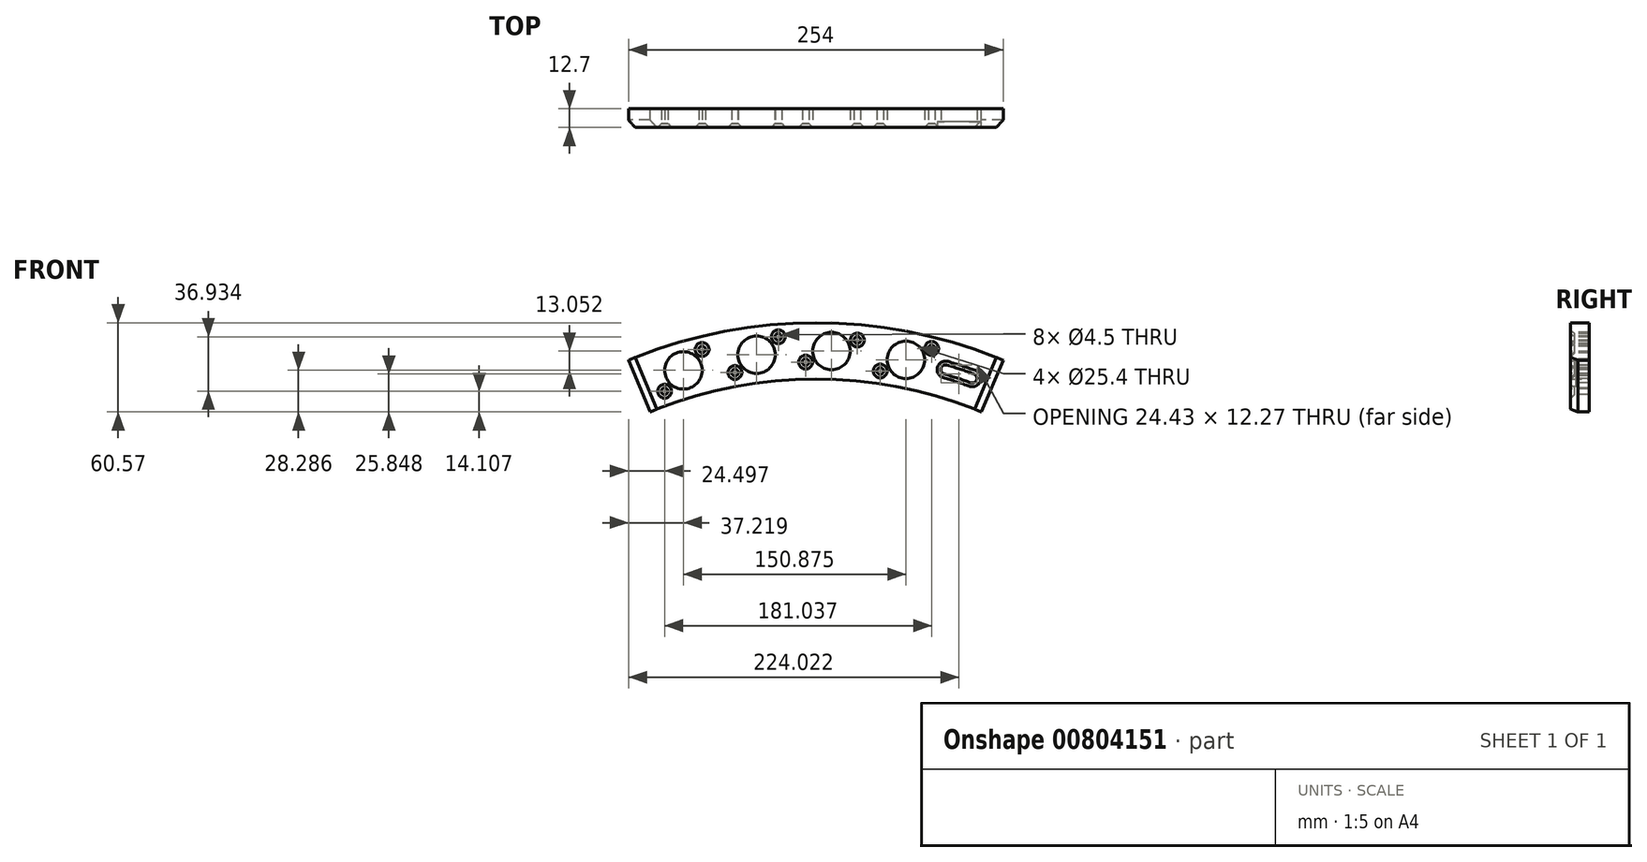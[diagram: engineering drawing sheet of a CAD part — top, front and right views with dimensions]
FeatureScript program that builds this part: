
annotation { "Feature Type Name" : "Feature", "Feature Type Description" : "" }
export const myFeature = defineFeature(function(context is Context, id is Id, definition is map)
    precondition{}
    {
        {
            var Q0;
            Q0=qCreatedBy(makeId("Front.planeOp"),FACE);
            var sketch = newSketch(context, id + "F0", { "sketchPlane" : qUnion([Q0])});
            skLineSegment(sketch, "E0", {"start": v(-127, 0) * mm, "end": v(127, 0) * mm, "construction": true});
            skArc(sketch, "E1", {"start": v(127, 0) * mm, "mid": v(0, 25.4) * mm, "end": v(-127, 0) * mm});
            skArc(sketch, "E2.0", {"start": v(112.35, -35.17) * mm, "mid": v(0, -12.7) * mm, "end": v(-112.35, -35.17) * mm});
            skLineSegment(sketch, "E3", {"start": v(-127, 0) * mm, "end": v(-112.35, -35.17) * mm});
            skLineSegment(sketch, "E4", {"start": v(127, 0) * mm, "end": v(112.35, -35.17) * mm});
            skSolve(sketch);
        }
        {
            var Q0;
            Q0=qSketchRegion(id+"F0",true);
            extrude(context, id + "F1", {"entities" : qUnion([Q0]), "depth" : 12.7 * mm, "offsetDistance" : 25.4 * mm});
        }
        {
            var Q0;
            Q0=makeQuery(id+"F1.opExtrude","CAP_FACE",FACE,{"disambiguationData":[OSD([sQuery(id+"F0.wireOp",EDGE,"E1"),sQuery(id+"F0.wireOp",EDGE,"E2.0"),sQuery(id+"F0.wireOp",EDGE,"E3"),sQuery(id+"F0.wireOp",EDGE,"E4")])],"isStart":false});
            var sketch = newSketch(context, id + "F2", { "sketchPlane" : qUnion([Q0])});
            skLineSegment(sketch, "E5", {"start": v(0, 25.4) * mm, "end": v(0, -12.7) * mm, "construction": true});
            skPoint(sketch, "E6", {"position": v(0, 6.35) * mm});
            skArc(sketch, "E7", {"start": v(119.67, -17.58) * mm, "mid": v(0, 6.35) * mm, "end": v(-119.67, -17.58) * mm, "construction": true});
            skCircle(sketch, "E8", {"center": v(61.1, 0.3) * mm, "radius": 12.7 * mm});
            skCircle(sketch, "E9", {"center": v(-89.78, -6.88) * mm, "radius": 12.7 * mm});
            skLineSegment(sketch, "E10", {"start": v(-119.67, -17.58) * mm, "end": v(-89.78, -6.88) * mm, "construction": true});
            skCircle(sketch, "E11", {"center": v(10.64, 6.17) * mm, "radius": 12.7 * mm});
            skCircle(sketch, "E12", {"center": v(-40.1, 3.75) * mm, "radius": 12.7 * mm});
            skLineSegment(sketch, "E13", {"start": v(-89.78, -6.88) * mm, "end": v(-40.1, 3.75) * mm, "construction": true});
            skLineSegment(sketch, "E14", {"start": v(10.64, 6.17) * mm, "end": v(61.1, 0.3) * mm, "construction": true});
            skLineSegment(sketch, "E15", {"start": v(-40.1, 3.75) * mm, "end": v(10.64, 6.17) * mm, "construction": true});
            skSolve(sketch);
        }
        {
            var Q0;
            Q0=qSketchRegion(id+"F2",true);
            extrude(context, id + "F3", {"entities" : qUnion([Q0]), "operationType" : NewBodyOperationType.REMOVE, "endBound" : BoundingType.THROUGH_ALL, "oppositeDirection" : true, "depth" : 25.4 * mm, "offsetDistance" : 25.4 * mm});
        }
        {
            var Q0;
            Q0=makeQuery(id+"F1.opExtrude","CAP_EDGE",EDGE,{"disambiguationData":[OSD([sQuery(id+"F0.wireOp",EDGE,"E3")])],"isStart":false});
            var Q1;
            Q1=makeQuery(id+"F1.opExtrude","CAP_EDGE",EDGE,{"disambiguationData":[OSD([sQuery(id+"F0.wireOp",EDGE,"E4")])],"isStart":false});
            chamfer(context, id + "F4", {"entities" : qUnion([Q0, Q1]), "width" : 5.08 * mm, "tangentPropagation" : true});
        }
        {
            var Q0;
            Q0=makeQuery(id+"F1.opExtrude","CAP_FACE",FACE,{"disambiguationData":[OSD([sQuery(id+"F0.wireOp",EDGE,"E1"),sQuery(id+"F0.wireOp",EDGE,"E2.0"),sQuery(id+"F0.wireOp",EDGE,"E3"),sQuery(id+"F0.wireOp",EDGE,"E4")])],"isStart":false});
            var sketch = newSketch(context, id + "F5", { "sketchPlane" : qUnion([Q0])});
            skCircle(sketch, "E16.0", {"center": v(10.64, 6.17) * mm, "radius": 12.7 * mm, "construction": true});
            skPoint(sketch, "E17", {"position": v(-6.88, -1.32) * mm});
            skLineSegment(sketch, "E18", {"start": v(10.64, 6.17) * mm, "end": v(-6.88, -1.32) * mm, "construction": true});
            skLineSegment(sketch, "E19", {"start": v(10.64, 6.17) * mm, "end": v(28.15, 13.66) * mm, "construction": true});
            skPoint(sketch, "E20", {"position": v(28.15, 13.66) * mm});
            skCircle(sketch, "E21.0", {"center": v(61.1, 0.3) * mm, "radius": 12.7 * mm});
            skLineSegment(sketch, "E22", {"start": v(61.1, 0.3) * mm, "end": v(78.53, 7.96) * mm, "construction": true});
            skLineSegment(sketch, "E23", {"start": v(61.1, 0.3) * mm, "end": v(43.66, -7.37) * mm, "construction": true});
            skPoint(sketch, "E24", {"position": v(43.66, -7.37) * mm});
            skPoint(sketch, "E25", {"position": v(78.53, 7.96) * mm});
            skCircle(sketch, "E26.1", {"center": v(-89.78, -6.88) * mm, "radius": 12.7 * mm});
            skCircle(sketch, "E26.2", {"center": v(-40.1, 3.75) * mm, "radius": 12.7 * mm});
            skLineSegment(sketch, "E27", {"start": v(-54.8, -8.36) * mm, "end": v(-40.1, 3.75) * mm});
            skLineSegment(sketch, "E28", {"start": v(-40.1, 3.75) * mm, "end": v(-25.4, 15.87) * mm});
            skLineSegment(sketch, "E29", {"start": v(-89.78, -6.88) * mm, "end": v(-102.5, -21.06) * mm});
            skLineSegment(sketch, "E30", {"start": v(-89.78, -6.88) * mm, "end": v(-77.06, 7.3) * mm});
            skPoint(sketch, "E31", {"position": v(-102.5, -21.06) * mm});
            skPoint(sketch, "E32", {"position": v(-77.06, 7.3) * mm});
            skPoint(sketch, "E33", {"position": v(-54.8, -8.36) * mm});
            skPoint(sketch, "E34", {"position": v(-25.4, 15.87) * mm});
            skSolve(sketch);
        }
        {
            var Q0;
            Q0=sQuery(id+"F5.wireOp",VERTEX,"E17");
            var Q1;
            Q1=sQuery(id+"F5.wireOp",VERTEX,"E20");
            var Q2;
            Q2=sQuery(id+"F5.wireOp",VERTEX,"E24");
            var Q3;
            Q3=sQuery(id+"F5.wireOp",VERTEX,"E25");
            var Q4;
            Q4=sQuery(id+"F5.wireOp",VERTEX,"E32");
            var Q5;
            Q5=sQuery(id+"F5.wireOp",VERTEX,"E31");
            var Q6;
            Q6=sQuery(id+"F5.wireOp",VERTEX,"E33");
            var Q7;
            Q7=sQuery(id+"F5.wireOp",VERTEX,"E34");
            var Q8;
            Q8=makeQuery(id+"F1.opExtrude","SWEPT_BODY",BODY,{"disambiguationData":[OSD([sQuery(id+"F0.wireOp",EDGE,"E1"),sQuery(id+"F0.wireOp",EDGE,"E2.0"),sQuery(id+"F0.wireOp",EDGE,"E3"),sQuery(id+"F0.wireOp",EDGE,"E4")])]});
            hole(context, id + "F6", {"style" : HoleStyle.C_SINK, "endStyle" : HoleEndStyle.THROUGH, "holeDiameter" : 4.5 * mm, "cSinkDiameter" : 9.4 * mm, "cSinkAngle" : 82 * degree, "majorDiameter" : 6.35 * mm, "tappedDepth" : 9.52 * mm, "tapClearance" : 3, "startFromSketch" : true, "locations" : qUnion([Q0, Q1, Q2, Q3, Q4, Q5, Q6, Q7]), "scope" : qUnion([Q8])});
        }
        {
            var Q0;
            Q0=makeQuery(id+"F1.opExtrude","CAP_FACE",FACE,{"disambiguationData":[OSD([sQuery(id+"F0.wireOp",EDGE,"E1"),sQuery(id+"F0.wireOp",EDGE,"E2.0"),sQuery(id+"F0.wireOp",EDGE,"E3"),sQuery(id+"F0.wireOp",EDGE,"E4")])],"isStart":false});
            var sketch = newSketch(context, id + "F7", { "sketchPlane" : qUnion([Q0])});
            skArc(sketch, "E35.0", {"start": v(114.97, -15.67) * mm, "mid": v(0.17, 6.35) * mm, "end": v(-114.66, -15.55) * mm, "construction": true});
            skLineSegment(sketch, "E36", {"start": v(107.64, -33.26) * mm, "end": v(114.97, -15.67) * mm, "construction": true});
            skArc(sketch, "E37.0", {"start": v(107.15, -9.3) * mm, "mid": v(98.05, -6.16) * mm, "end": v(88.86, -3.3) * mm});
            skArc(sketch, "E38.0", {"start": v(113.8, -18.62) * mm, "mid": v(113.77, -18.6) * mm, "end": v(113.75, -18.6) * mm, "construction": true});
            skArc(sketch, "E39", {"start": v(90.98, -7.33) * mm, "mid": v(91, -7.3) * mm, "end": v(91, -7.26) * mm});
            skArc(sketch, "E40", {"start": v(103.07, -11.22) * mm, "mid": v(103.06, -11.26) * mm, "end": v(103.05, -11.3) * mm});
            skLineSegment(sketch, "E41", {"start": v(87.96, -6.34) * mm, "end": v(106.06, -12.29) * mm, "construction": true});
            skArc(sketch, "E42.trimOffspring", {"start": v(104.98, -15.27) * mm, "mid": v(96.07, -12.2) * mm, "end": v(87.07, -9.39) * mm});
            skArc(sketch, "E43.trimOffspring", {"start": v(88.86, -3.3) * mm, "mid": v(84.92, -5.45) * mm, "end": v(87.07, -9.39) * mm});
            skArc(sketch, "E44.trimOffspring", {"start": v(104.98, -15.27) * mm, "mid": v(109.05, -13.37) * mm, "end": v(107.15, -9.3) * mm});
            skLineSegment(sketch, "E45", {"start": v(106.06, -12.29) * mm, "end": v(114.97, -15.67) * mm, "construction": true});
            skSolve(sketch);
        }
        {
            var Q0;
            Q0 = qSketchRegion(id + "F7", true);
            extrude(context, id + "F8", {"entities" : qUnion([Q0]), "operationType" : NewBodyOperationType.REMOVE, "endBound" : BoundingType.THROUGH_ALL, "oppositeDirection" : true, "depth" : 25.4 * mm, "offsetDistance" : 25.4 * mm});
        }
        {
            var Q0;
            Q0=makeQuery(id+"F1.opExtrude","CAP_FACE",FACE,{"disambiguationData":[OSD([sQuery(id+"F0.wireOp",EDGE,"E1"),sQuery(id+"F0.wireOp",EDGE,"E2.0"),sQuery(id+"F0.wireOp",EDGE,"E3"),sQuery(id+"F0.wireOp",EDGE,"E4")])],"isStart":false});
            var sketch = newSketch(context, id + "F9", { "sketchPlane" : qUnion([Q0])});
            skArc(sketch, "E46.0", {"start": v(107.15, -9.3) * mm, "mid": v(98.05, -6.16) * mm, "end": v(88.86, -3.3) * mm});
            skArc(sketch, "E46.1", {"start": v(104.98, -15.27) * mm, "mid": v(109.05, -13.37) * mm, "end": v(107.15, -9.3) * mm});
            skArc(sketch, "E46.2", {"start": v(104.98, -15.27) * mm, "mid": v(96.07, -12.2) * mm, "end": v(87.07, -9.39) * mm});
            skArc(sketch, "E46.3", {"start": v(88.86, -3.3) * mm, "mid": v(84.92, -5.45) * mm, "end": v(87.07, -9.39) * mm});
            skArc(sketch, "E47.0", {"start": v(89.58, -0.86) * mm, "mid": v(82.48, -4.73) * mm, "end": v(86.35, -11.83) * mm});
            skArc(sketch, "E47.1", {"start": v(108.01, -6.91) * mm, "mid": v(98.84, -3.75) * mm, "end": v(89.58, -0.86) * mm});
            skArc(sketch, "E47.2", {"start": v(104.12, -17.66) * mm, "mid": v(111.44, -14.23) * mm, "end": v(108.01, -6.91) * mm});
            skArc(sketch, "E47.3", {"start": v(104.12, -17.66) * mm, "mid": v(95.28, -14.6) * mm, "end": v(86.35, -11.83) * mm});
            skSolve(sketch);
        }
        {
            var Q0;
            Q0=makeQuery(id+"F9.imprint","IMPRINT",FACE,{"disambiguationData":[TD([[makeQuery(id+"F9.imprint","IMPRINT",EDGE,{"derivedFrom":sQuery(id+"F9.wireOp",EDGE,"E46.0")}),-1.0]])]});
            extrude(context, id + "F10", {"entities" : qUnion([Q0]), "operationType" : NewBodyOperationType.REMOVE, "oppositeDirection" : true, "depth" : 3.8 * mm, "offsetDistance" : 25.4 * mm});
        }
    });
